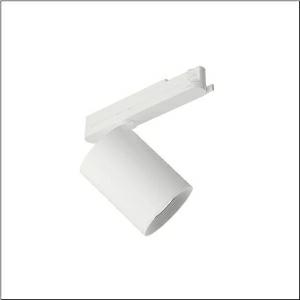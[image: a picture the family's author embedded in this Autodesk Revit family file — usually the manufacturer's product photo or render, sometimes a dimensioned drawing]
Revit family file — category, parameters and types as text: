
# Revit family: spot_21_51se13mba5b
name_source: partatom
category: Lighting Fixtures
units: mm (PartAtom-declared; Revit-internal decimal feet)

## family parameters
Cut with Voids When Loaded = No
Host = Face
Light Source = No
Part Type = Normal
Room Calculation Point = No
Round Connector Dimension = Use Diameter
Shared = No

## types (1)
- --- (1 x LED, 5300 lm, 41.8 W, 2700K)
    Apparent Load = 42 VA
    CIE Flux Codes = 95 98 99 100 100
    Color Rendering = 90
    Color Temperature = 2700K
    Default Elevation = 1800 mm
    Description = Spot 21, directional spotlight, light control with lens, of PMMA, LED rated luminous flux: 5.090lm, light colour: 927, control gear: ECG Multilumen, with 3-phase adapter, mains connection: 220..240V, AC, 50/60Hz, of aluminium, traffic white (RAL 9016), length: 213mm, diameter: 105mm, protection rating (complete): IP20, insulation class (complete): insulation class I (protective earthing), certification: CE, impact resistance: IK02, permissible ambient temperature for indoor applications: -20..+40°C, packaging unit: 1 piece
    Height = 175 mm
    Lamp = 1 x LED
    Lamp Light Flux = 5300 lm
    Lamp Power = 41.8 W
    Lamp count = 1
    Length = 105 mm
    Luminous efficacy = 127 lm/W
    Manufacturer = Siteco
    ModVariant = No
    Model = 51SE13MBA5B
    Mounting Place = Ceiling
    Mounting Type = Pendant
    Number of Poles = 1
    OnlyDefault = Yes
    Power Factor = 1
    Product Name = Spot 21
    Product group = directional spotlight
    ProductGroupID = 904
    Protection Class = Protection class I
    Protection Degree = IP 20
    RLX_Detail_Level = 1
    RlxData = <blob elided: 17609 chars, md5=7fedff68>
    Socket = socket
    Standby Power = 0 W
    System Light Flux = 5300 lm
    System Power = 42 W
    Type Comments = factory setting: luminous flux: 100 % | (ON | ON | ON | ON) | 1050 mA
    Type Image = l_1003976.jpg
    URL = http://relux.com
    VarID = @adj_053405
    Voltage = 0 V
    Weight = 0.00 kg
    Width = 0 mm  [stored 0 ft]

note: [stored X ft] marks values corroborated as IEEE doubles in the binary element streams (Revit-internal decimal feet)

## geometry (parser evidence)
native form markers: Blend x4, Sweep x12
no freeform markers — native parametric forms only
